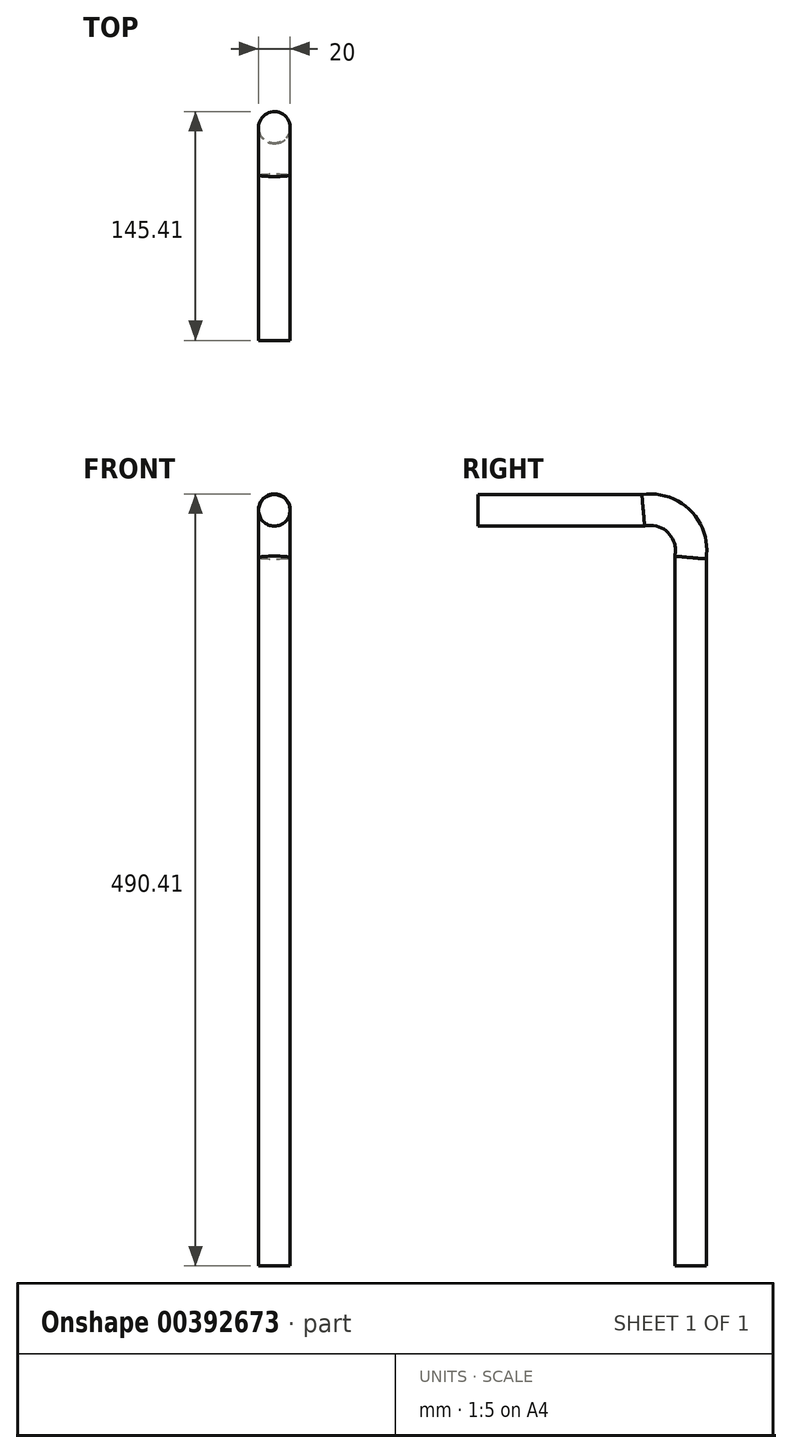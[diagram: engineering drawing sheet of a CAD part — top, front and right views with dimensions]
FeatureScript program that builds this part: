
annotation { "Feature Type Name" : "Feature", "Feature Type Description" : "" }
export const myFeature = defineFeature(function(context is Context, id is Id, definition is map)
    precondition{}
    {
        {
            var Q0;
            Q0=qCreatedBy(makeId("Front.planeOp"),FACE);
            var sketch = newSketch(context, id + "F0", { "sketchPlane" : qUnion([Q0])});
            skCircle(sketch, "E0", {"center": v(0, 0) * mm, "radius": 10 * mm});
            skSolve(sketch);
        }
        {
            var Q0;
            Q0=qCreatedBy(makeId("Right.planeOp"),FACE);
            var sketch = newSketch(context, id + "F1", { "sketchPlane" : qUnion([Q0])});
            skArc(sketch, "E1", {"start": v(135, -30) * mm, "mid": v(127.86, -7.14) * mm, "end": v(105, 0) * mm});
            skLineSegment(sketch, "E2", {"start": v(105, 0) * mm, "end": v(0, 0) * mm});
            skLineSegment(sketch, "E3", {"start": v(135, -30) * mm, "end": v(135, -480) * mm});
            skSolve(sketch);
        }
        {
            var Q0;
            Q0=makeQuery(id+"F0.imprint","IMPRINT",FACE,{"disambiguationData":[TD([[makeQuery(id+"F0.imprint","IMPRINT",EDGE,{"derivedFrom":sQuery(id+"F0.wireOp",EDGE,"E0")}),1.0]])]});
            var Q1;
            Q1=sQuery(id+"F1.wireOp",EDGE,"E2");
            var Q2;
            Q2=sQuery(id+"F1.wireOp",EDGE,"E1");
            var Q3;
            Q3=sQuery(id+"F1.wireOp",EDGE,"E3");
            sweep(context, id + "F2", {"profiles" : qUnion([Q0]), "path" : qUnion([Q1, Q2, Q3])});
        }
    });
